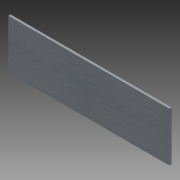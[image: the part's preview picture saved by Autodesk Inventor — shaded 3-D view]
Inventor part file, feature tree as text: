
AUTODESK INVENTOR PART (.ipt)
format: ipt  version: 2011 SP1 (Build 150282100, 282)  size: 79,872 bytes
history: native  units: in
note: dims shown in document units (in); Inventor stores cm internally (conversion verified against a paired STEP export)
features: extrude x1, sketch x1
ambient origin geometry x8: Origin, YZ Plane, XZ Plane, XY Plane, X Axis, Y Axis, Z Axis, Center Point
bodies: Solid1 (feature_tree)
feature tree (2):
  extrude  "Extrusion1"  Depth=4.5in
  sketch  "Sketch1"  dims[d0=9.0in d1=4.5in d2=2.75in d3=1.375in d4=0.125in d5=0.0in]
